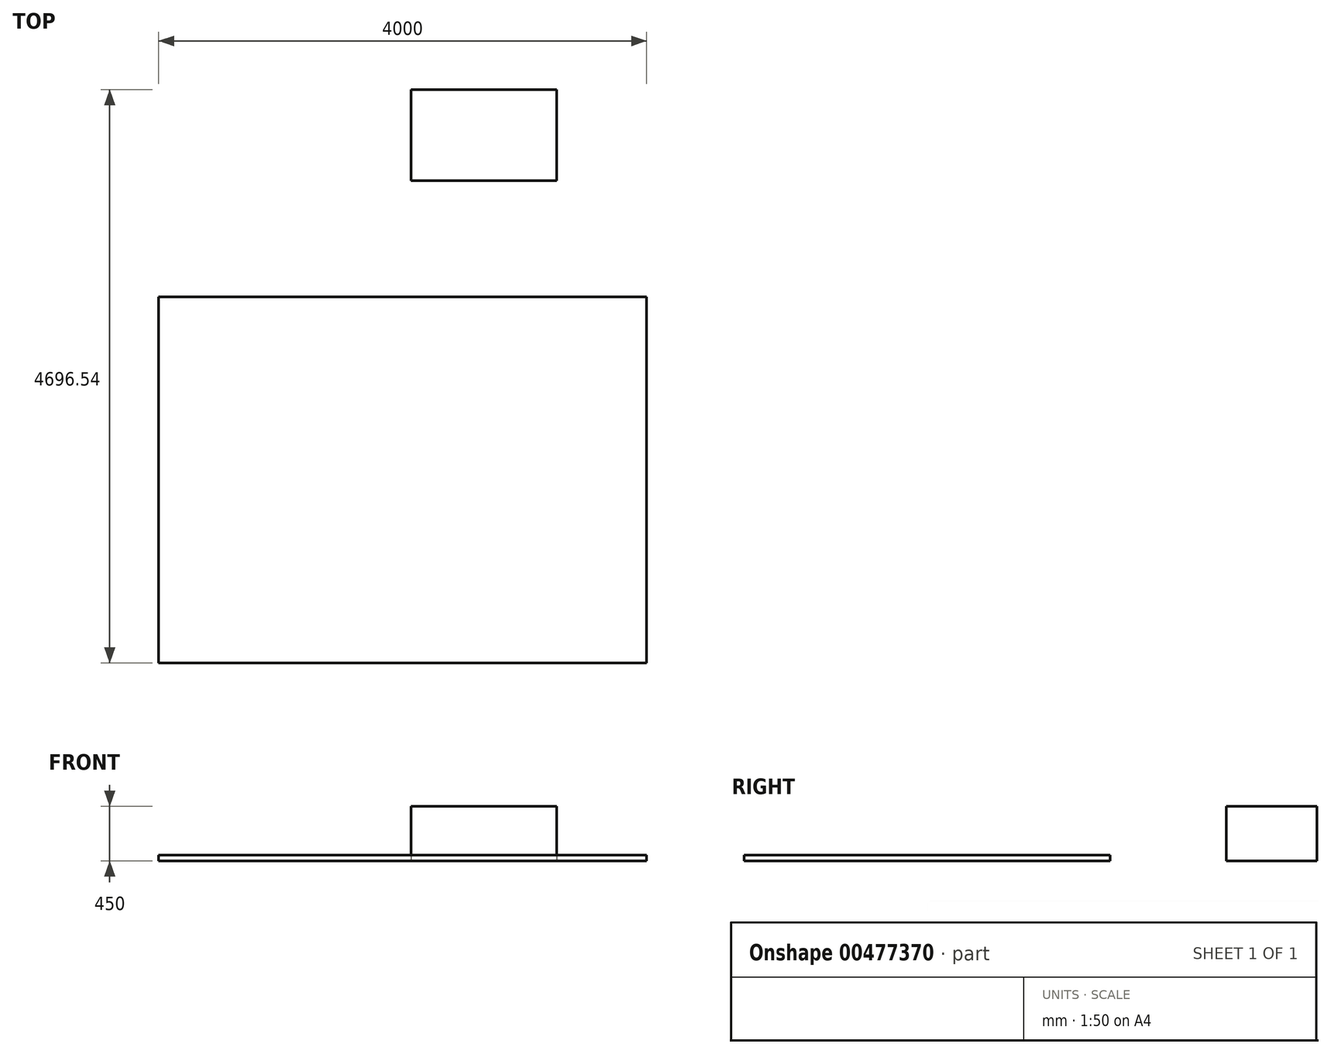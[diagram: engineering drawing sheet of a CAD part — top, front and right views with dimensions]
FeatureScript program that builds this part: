
annotation { "Feature Type Name" : "Feature", "Feature Type Description" : "" }
export const myFeature = defineFeature(function(context is Context, id is Id, definition is map)
    precondition{}
    {
        {
            var Q0;
            Q0=qCreatedBy(makeId("Top.planeOp"),FACE);
            var sketch = newSketch(context, id + "F0", { "sketchPlane" : qUnion([Q0])});
            skLineSegment(sketch, "E0.bottom", {"start": v(597, -372) * mm, "end": v(-597, -372) * mm});
            skLineSegment(sketch, "E0.top", {"start": v(597, 372) * mm, "end": v(-597, 372) * mm});
            skLineSegment(sketch, "E0.left", {"start": v(597, -372) * mm, "end": v(597, 372) * mm});
            skLineSegment(sketch, "E0.right", {"start": v(-597, -372) * mm, "end": v(-597, 372) * mm});
            skPoint(sketch, "E0.middle", {"position": v(0, 0) * mm});
            skSolve(sketch);
        }
        {
            var Q0;
            Q0 = qSketchRegion(id + "F0", true);
            extrude(context, id + "F1", {"entities" : qUnion([Q0]), "depth" : 450 * mm});
        }
        {
            var Q0;
            Q0=qCreatedBy(makeId("Top.planeOp"),FACE);
            var sketch = newSketch(context, id + "F2", { "sketchPlane" : qUnion([Q0])});
            skLineSegment(sketch, "E1.bottom", {"start": v(-2666.9, -1324.54) * mm, "end": v(1333.1, -1324.54) * mm});
            skLineSegment(sketch, "E1.top", {"start": v(-2666.9, -4324.54) * mm, "end": v(1333.1, -4324.54) * mm});
            skLineSegment(sketch, "E1.left", {"start": v(-2666.9, -1324.54) * mm, "end": v(-2666.9, -4324.54) * mm});
            skLineSegment(sketch, "E1.right", {"start": v(1333.1, -1324.54) * mm, "end": v(1333.1, -4324.54) * mm});
            skSolve(sketch);
        }
        {
            var Q0;
            Q0=makeQuery(id+"F2.imprint","IMPRINT",FACE,{"disambiguationData":[TD([[makeQuery(id+"F2.imprint","IMPRINT",EDGE,{"derivedFrom":sQuery(id+"F2.wireOp",EDGE,"E1.bottom")}),-1.0]])]});
            extrude(context, id + "F3", {"entities" : qUnion([Q0]), "depth" : 50 * mm});
        }
    });
